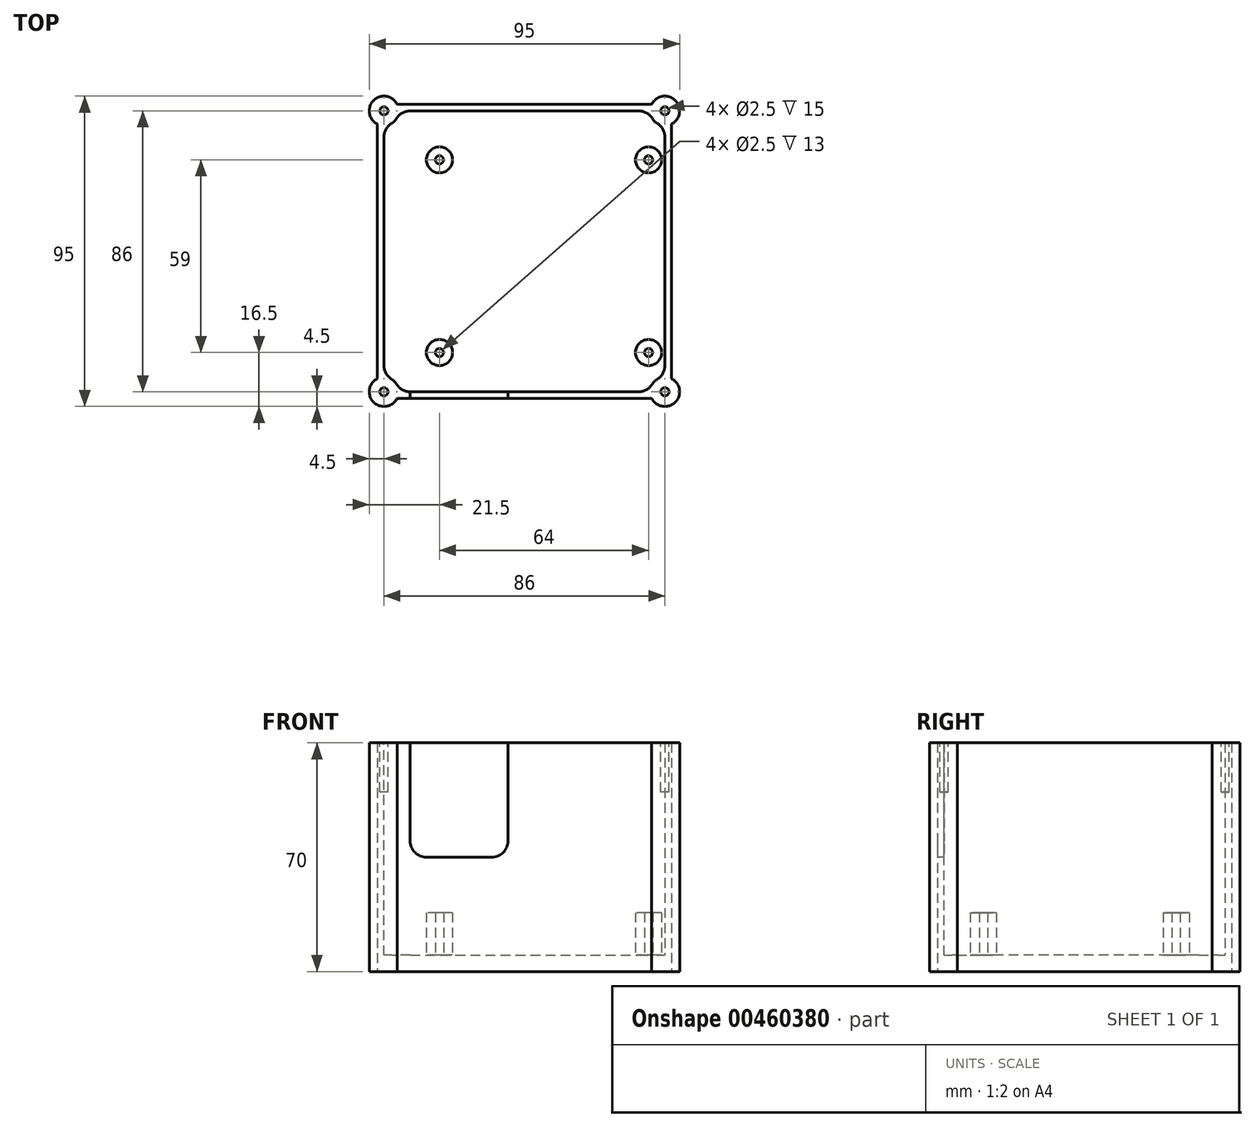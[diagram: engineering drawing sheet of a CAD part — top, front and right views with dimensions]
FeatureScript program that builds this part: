
annotation { "Feature Type Name" : "Feature", "Feature Type Description" : "" }
export const myFeature = defineFeature(function(context is Context, id is Id, definition is map)
    precondition{}
    {
        {
            var Q0;
            Q0=qCreatedBy(makeId("Top.planeOp"),FACE);
            var sketch = newSketch(context, id + "F0", { "sketchPlane" : qUnion([Q0])});
            skLineSegment(sketch, "E0.bottom", {"start": v(0, 0) * mm, "end": v(90, 0) * mm});
            skLineSegment(sketch, "E0.top", {"start": v(0, 90) * mm, "end": v(90, 90) * mm});
            skLineSegment(sketch, "E0.left", {"start": v(0, 0) * mm, "end": v(0, 90) * mm});
            skLineSegment(sketch, "E0.right", {"start": v(90, 0) * mm, "end": v(90, 90) * mm});
            skSolve(sketch);
        }
        {
            var Q0;
            Q0 = qSketchRegion(id + "F0", true);
            extrude(context, id + "F1", {"entities" : qUnion([Q0]), "depth" : 70 * mm});
        }
        {
            var Q0;
            Q0=makeQuery(id+"F1.opExtrude","CAP_FACE",FACE,{"disambiguationData":[OSD([sQuery(id+"F0.wireOp",EDGE,"E0.bottom"),sQuery(id+"F0.wireOp",EDGE,"E0.top"),sQuery(id+"F0.wireOp",EDGE,"E0.left"),sQuery(id+"F0.wireOp",EDGE,"E0.right")])],"isStart":false});
            var sketch = newSketch(context, id + "F2", { "sketchPlane" : qUnion([Q0])});
            skLineSegment(sketch, "E1.bottom", {"start": v(2, 88) * mm, "end": v(88, 88) * mm});
            skLineSegment(sketch, "E1.top", {"start": v(2, 2) * mm, "end": v(88, 2) * mm});
            skLineSegment(sketch, "E1.left", {"start": v(2, 88) * mm, "end": v(2, 2) * mm});
            skLineSegment(sketch, "E1.right", {"start": v(88, 88) * mm, "end": v(88, 2) * mm});
            skLineSegment(sketch, "E2.bottom", {"start": v(2, 88) * mm, "end": v(88, 88) * mm, "construction": true});
            skLineSegment(sketch, "E2.top", {"start": v(2, 2) * mm, "end": v(88, 2) * mm, "construction": true});
            skLineSegment(sketch, "E2.left", {"start": v(2, 88) * mm, "end": v(2, 2) * mm, "construction": true});
            skLineSegment(sketch, "E2.right", {"start": v(88, 88) * mm, "end": v(88, 2) * mm, "construction": true});
            skSolve(sketch);
        }
        {
            var Q0;
            Q0 = qSketchRegion(id + "F2", true);
            extrude(context, id + "F3", {"entities" : qUnion([Q0]), "operationType" : NewBodyOperationType.REMOVE, "oppositeDirection" : true, "depth" : 65 * mm});
        }
        {
            var Q0;
            Q0=qCreatedBy(makeId("Top.planeOp"),FACE);
            var sketch = newSketch(context, id + "F4", { "sketchPlane" : qUnion([Q0])});
            skLineSegment(sketch, "E3.bottom", {"start": v(2, 88) * mm, "end": v(88, 88) * mm, "construction": true});
            skLineSegment(sketch, "E3.top", {"start": v(2, 2) * mm, "end": v(88, 2) * mm, "construction": true});
            skLineSegment(sketch, "E3.left", {"start": v(2, 88) * mm, "end": v(2, 2) * mm, "construction": true});
            skLineSegment(sketch, "E3.right", {"start": v(88, 88) * mm, "end": v(88, 2) * mm, "construction": true});
            skCircle(sketch, "E4", {"center": v(2, 88) * mm, "radius": 4.5 * mm});
            skCircle(sketch, "E5", {"center": v(88, 88) * mm, "radius": 4.5 * mm});
            skCircle(sketch, "E6", {"center": v(2, 2) * mm, "radius": 4.5 * mm});
            skCircle(sketch, "E7", {"center": v(88, 2) * mm, "radius": 4.5 * mm});
            skSolve(sketch);
        }
        {
            var Q0;
            Q0 = qSketchRegion(id + "F4", true);
            extrude(context, id + "F5", {"entities" : qUnion([Q0]), "operationType" : NewBodyOperationType.ADD, "depth" : 70 * mm});
        }
        {
            var Q0;
            Q0=qCreatedBy(makeId("Front.planeOp"),FACE);
            var sketch = newSketch(context, id + "F6", { "sketchPlane" : qUnion([Q0])});
            skLineSegment(sketch, "E8.bottom", {"start": v(10, 70) * mm, "end": v(40, 70) * mm});
            skLineSegment(sketch, "E8.top", {"start": v(10, 35) * mm, "end": v(40, 35) * mm});
            skLineSegment(sketch, "E8.left", {"start": v(10, 70) * mm, "end": v(10, 35) * mm});
            skLineSegment(sketch, "E8.right", {"start": v(40, 70) * mm, "end": v(40, 35) * mm});
            skSolve(sketch);
        }
        {
            var Q0;
            Q0 = qSketchRegion(id + "F6", true);
            extrude(context, id + "F7", {"entities" : qUnion([Q0]), "operationType" : NewBodyOperationType.REMOVE, "endBound" : BoundingType.UP_TO_NEXT, "oppositeDirection" : true, "depth" : 25 * mm});
        }
        {
            var Q0;
            Q0=makeQuery(id+"F5.boolean.opBoolean","MERGE",FACE,{"derivedFrom":[makeQuery(id+"F1.opExtrude","CAP_FACE",FACE,{"disambiguationData":[OSD([sQuery(id+"F0.wireOp",EDGE,"E0.bottom"),sQuery(id+"F0.wireOp",EDGE,"E0.top"),sQuery(id+"F0.wireOp",EDGE,"E0.left"),sQuery(id+"F0.wireOp",EDGE,"E0.right")])],"isStart":false}),makeQuery(id+"F5.opExtrude","CAP_FACE",FACE,{"disambiguationData":[OSD([sQuery(id+"F4.wireOp",EDGE,"E4")])],"isStart":false}),makeQuery(id+"F5.opExtrude","CAP_FACE",FACE,{"disambiguationData":[OSD([sQuery(id+"F4.wireOp",EDGE,"E5")])],"isStart":false}),makeQuery(id+"F5.opExtrude","CAP_FACE",FACE,{"disambiguationData":[OSD([sQuery(id+"F4.wireOp",EDGE,"E6")])],"isStart":false}),makeQuery(id+"F5.opExtrude","CAP_FACE",FACE,{"disambiguationData":[OSD([sQuery(id+"F4.wireOp",EDGE,"E7")])],"isStart":false})]});
            var sketch = newSketch(context, id + "F8", { "sketchPlane" : qUnion([Q0])});
            skLineSegment(sketch, "E9.bottom", {"start": v(2, 88) * mm, "end": v(88, 88) * mm, "construction": true});
            skLineSegment(sketch, "E9.top", {"start": v(2, 2) * mm, "end": v(88, 2) * mm, "construction": true});
            skLineSegment(sketch, "E9.left", {"start": v(2, 88) * mm, "end": v(2, 2) * mm, "construction": true});
            skLineSegment(sketch, "E9.right", {"start": v(88, 88) * mm, "end": v(88, 2) * mm, "construction": true});
            skCircle(sketch, "E10", {"center": v(2, 88) * mm, "radius": 1.25 * mm});
            skCircle(sketch, "E11", {"center": v(88, 88) * mm, "radius": 1.25 * mm});
            skCircle(sketch, "E12", {"center": v(2, 2) * mm, "radius": 1.25 * mm});
            skCircle(sketch, "E13", {"center": v(88, 2) * mm, "radius": 1.25 * mm});
            skSolve(sketch);
        }
        {
            var Q0;
            Q0 = qSketchRegion(id + "F8", true);
            extrude(context, id + "F9", {"entities" : qUnion([Q0]), "operationType" : NewBodyOperationType.REMOVE, "oppositeDirection" : true, "depth" : 15 * mm});
        }
        {
            var Q0;
            Q0=makeQuery(id+"F3.boolean.opBoolean","COPY",FACE,{"derivedFrom":makeQuery(id+"F3.opExtrude","CAP_FACE",FACE,{"disambiguationData":[OSD([sQuery(id+"F2.wireOp",EDGE,"E1.bottom"),sQuery(id+"F2.wireOp",EDGE,"E1.top"),sQuery(id+"F2.wireOp",EDGE,"E1.left"),sQuery(id+"F2.wireOp",EDGE,"E1.right")])],"isStart":false})});
            var sketch = newSketch(context, id + "F10", { "sketchPlane" : qUnion([Q0])});
            skLineSegment(sketch, "E14.bottom", {"start": v(16, 76) * mm, "end": v(86, 76) * mm, "construction": true});
            skLineSegment(sketch, "E14.top", {"start": v(16, 11) * mm, "end": v(86, 11) * mm, "construction": true});
            skLineSegment(sketch, "E14.left", {"start": v(16, 76) * mm, "end": v(16, 11) * mm, "construction": true});
            skLineSegment(sketch, "E14.right", {"start": v(86, 76) * mm, "end": v(86, 11) * mm, "construction": true});
            skLineSegment(sketch, "E15.bottom", {"start": v(19, 73) * mm, "end": v(83, 73) * mm, "construction": true});
            skLineSegment(sketch, "E15.top", {"start": v(19, 14) * mm, "end": v(83, 14) * mm, "construction": true});
            skLineSegment(sketch, "E15.left", {"start": v(19, 73) * mm, "end": v(19, 14) * mm, "construction": true});
            skLineSegment(sketch, "E15.right", {"start": v(83, 73) * mm, "end": v(83, 14) * mm, "construction": true});
            skCircle(sketch, "E16", {"center": v(19, 73) * mm, "radius": 4 * mm});
            skCircle(sketch, "E17", {"center": v(83, 73) * mm, "radius": 4 * mm});
            skCircle(sketch, "E18", {"center": v(83, 14) * mm, "radius": 4 * mm});
            skCircle(sketch, "E19", {"center": v(19, 14) * mm, "radius": 4 * mm});
            skCircle(sketch, "E20", {"center": v(19, 73) * mm, "radius": 1.25 * mm});
            skCircle(sketch, "E21", {"center": v(83, 73) * mm, "radius": 1.25 * mm});
            skCircle(sketch, "E22", {"center": v(83, 14) * mm, "radius": 1.25 * mm});
            skCircle(sketch, "E23", {"center": v(19, 14) * mm, "radius": 1.25 * mm});
            skSolve(sketch);
        }
        {
            var Q0;
            Q0 = qSketchRegion(id + "F10", true);
            extrude(context, id + "F11", {"entities" : qUnion([Q0]), "operationType" : NewBodyOperationType.ADD, "depth" : 13 * mm});
        }
        {
            var Q0;
            Q0=makeQuery(id+"F3.boolean.opBoolean","COPY",EDGE,{"derivedFrom":makeQuery(id+"F3.opExtrude","SWEPT_EDGE",EDGE,{"disambiguationData":[OSD([sQuery(id+"F2.wireOp",EDGE,"E1.top"),sQuery(id+"F2.wireOp",EDGE,"E1.right")])]})});
            var Q1;
            Q1=makeQuery(id+"F3.boolean.opBoolean","COPY",EDGE,{"derivedFrom":makeQuery(id+"F3.opExtrude","SWEPT_EDGE",EDGE,{"disambiguationData":[OSD([sQuery(id+"F2.wireOp",EDGE,"E1.bottom"),sQuery(id+"F2.wireOp",EDGE,"E1.right")])]})});
            var Q2;
            Q2=makeQuery(id+"F3.boolean.opBoolean","COPY",EDGE,{"derivedFrom":makeQuery(id+"F3.opExtrude","SWEPT_EDGE",EDGE,{"disambiguationData":[OSD([sQuery(id+"F2.wireOp",EDGE,"E1.bottom"),sQuery(id+"F2.wireOp",EDGE,"E1.left")])]})});
            var Q3;
            Q3=makeQuery(id+"F3.boolean.opBoolean","COPY",EDGE,{"derivedFrom":makeQuery(id+"F3.opExtrude","SWEPT_EDGE",EDGE,{"disambiguationData":[OSD([sQuery(id+"F2.wireOp",EDGE,"E1.top"),sQuery(id+"F2.wireOp",EDGE,"E1.left")])]})});
            var Q4;
            Q4=makeQuery(id+"F7.boolean.opBoolean","COPY",EDGE,{"derivedFrom":makeQuery(id+"F7.opExtrude","SWEPT_EDGE",EDGE,{"disambiguationData":[OSD([sQuery(id+"F6.wireOp",EDGE,"E8.top"),sQuery(id+"F6.wireOp",EDGE,"E8.right")])]})});
            var Q5;
            Q5=makeQuery(id+"F7.boolean.opBoolean","COPY",EDGE,{"derivedFrom":makeQuery(id+"F7.opExtrude","SWEPT_EDGE",EDGE,{"disambiguationData":[OSD([sQuery(id+"F6.wireOp",EDGE,"E8.top"),sQuery(id+"F6.wireOp",EDGE,"E8.left")])]})});
            fillet(context, id + "F12", {"entities" : qUnion([Q0, Q1, Q2, Q3, Q4, Q5]), "radius" : 5 * mm, "tangentPropagation" : true, "allowEdgeOverflow" : false});
        }
        {
            var Q0;
            Q0=makeQuery(id+"F5.boolean.opBoolean","INTERSECT",EDGE,{"derivedFrom":[makeQuery(id+"F3.boolean.opBoolean","COPY",FACE,{"derivedFrom":makeQuery(id+"F3.opExtrude","SWEPT_FACE",FACE,{"disambiguationData":[OSD([sQuery(id+"F2.wireOp",EDGE,"E1.bottom")])]})}),makeQuery(id+"F5.opExtrude","SWEPT_FACE",FACE,{"disambiguationData":[OSD([sQuery(id+"F4.wireOp",EDGE,"E4")])]})]});
            var Q1;
            Q1=makeQuery(id+"F5.boolean.opBoolean","INTERSECT",EDGE,{"derivedFrom":[makeQuery(id+"F3.boolean.opBoolean","COPY",FACE,{"derivedFrom":makeQuery(id+"F3.opExtrude","SWEPT_FACE",FACE,{"disambiguationData":[OSD([sQuery(id+"F2.wireOp",EDGE,"E1.left")])]})}),makeQuery(id+"F5.opExtrude","SWEPT_FACE",FACE,{"disambiguationData":[OSD([sQuery(id+"F4.wireOp",EDGE,"E4")])]})]});
            var Q2;
            Q2=makeQuery(id+"F5.boolean.opBoolean","INTERSECT",EDGE,{"derivedFrom":[makeQuery(id+"F3.boolean.opBoolean","COPY",FACE,{"derivedFrom":makeQuery(id+"F3.opExtrude","SWEPT_FACE",FACE,{"disambiguationData":[OSD([sQuery(id+"F2.wireOp",EDGE,"E1.right")])]})}),makeQuery(id+"F5.opExtrude","SWEPT_FACE",FACE,{"disambiguationData":[OSD([sQuery(id+"F4.wireOp",EDGE,"E5")])]})]});
            var Q3;
            Q3=makeQuery(id+"F5.boolean.opBoolean","INTERSECT",EDGE,{"derivedFrom":[makeQuery(id+"F3.boolean.opBoolean","COPY",FACE,{"derivedFrom":makeQuery(id+"F3.opExtrude","SWEPT_FACE",FACE,{"disambiguationData":[OSD([sQuery(id+"F2.wireOp",EDGE,"E1.bottom")])]})}),makeQuery(id+"F5.opExtrude","SWEPT_FACE",FACE,{"disambiguationData":[OSD([sQuery(id+"F4.wireOp",EDGE,"E5")])]})]});
            var Q4;
            Q4=makeQuery(id+"F5.boolean.opBoolean","INTERSECT",EDGE,{"derivedFrom":[makeQuery(id+"F3.boolean.opBoolean","COPY",FACE,{"derivedFrom":makeQuery(id+"F3.opExtrude","SWEPT_FACE",FACE,{"disambiguationData":[OSD([sQuery(id+"F2.wireOp",EDGE,"E1.left")])]})}),makeQuery(id+"F5.opExtrude","SWEPT_FACE",FACE,{"disambiguationData":[OSD([sQuery(id+"F4.wireOp",EDGE,"E6")])]})]});
            var Q5;
            Q5=makeQuery(id+"F5.boolean.opBoolean","INTERSECT",EDGE,{"derivedFrom":[makeQuery(id+"F3.boolean.opBoolean","COPY",FACE,{"derivedFrom":makeQuery(id+"F3.opExtrude","SWEPT_FACE",FACE,{"disambiguationData":[OSD([sQuery(id+"F2.wireOp",EDGE,"E1.top")])]})}),makeQuery(id+"F5.opExtrude","SWEPT_FACE",FACE,{"disambiguationData":[OSD([sQuery(id+"F4.wireOp",EDGE,"E6")])]})]});
            var Q6;
            Q6=makeQuery(id+"F5.boolean.opBoolean","INTERSECT",EDGE,{"derivedFrom":[makeQuery(id+"F3.boolean.opBoolean","COPY",FACE,{"derivedFrom":makeQuery(id+"F3.opExtrude","SWEPT_FACE",FACE,{"disambiguationData":[OSD([sQuery(id+"F2.wireOp",EDGE,"E1.right")])]})}),makeQuery(id+"F5.opExtrude","SWEPT_FACE",FACE,{"disambiguationData":[OSD([sQuery(id+"F4.wireOp",EDGE,"E7")])]})]});
            var Q7;
            Q7=makeQuery(id+"F5.boolean.opBoolean","INTERSECT",EDGE,{"derivedFrom":[makeQuery(id+"F3.boolean.opBoolean","COPY",FACE,{"derivedFrom":makeQuery(id+"F3.opExtrude","SWEPT_FACE",FACE,{"disambiguationData":[OSD([sQuery(id+"F2.wireOp",EDGE,"E1.top")])]})}),makeQuery(id+"F5.opExtrude","SWEPT_FACE",FACE,{"disambiguationData":[OSD([sQuery(id+"F4.wireOp",EDGE,"E7")])]})]});
            fillet(context, id + "F13", {"entities" : qUnion([Q0, Q1, Q2, Q3, Q4, Q5, Q6, Q7]), "radius" : 5 * mm, "tangentPropagation" : true, "allowEdgeOverflow" : false});
        }
    });
